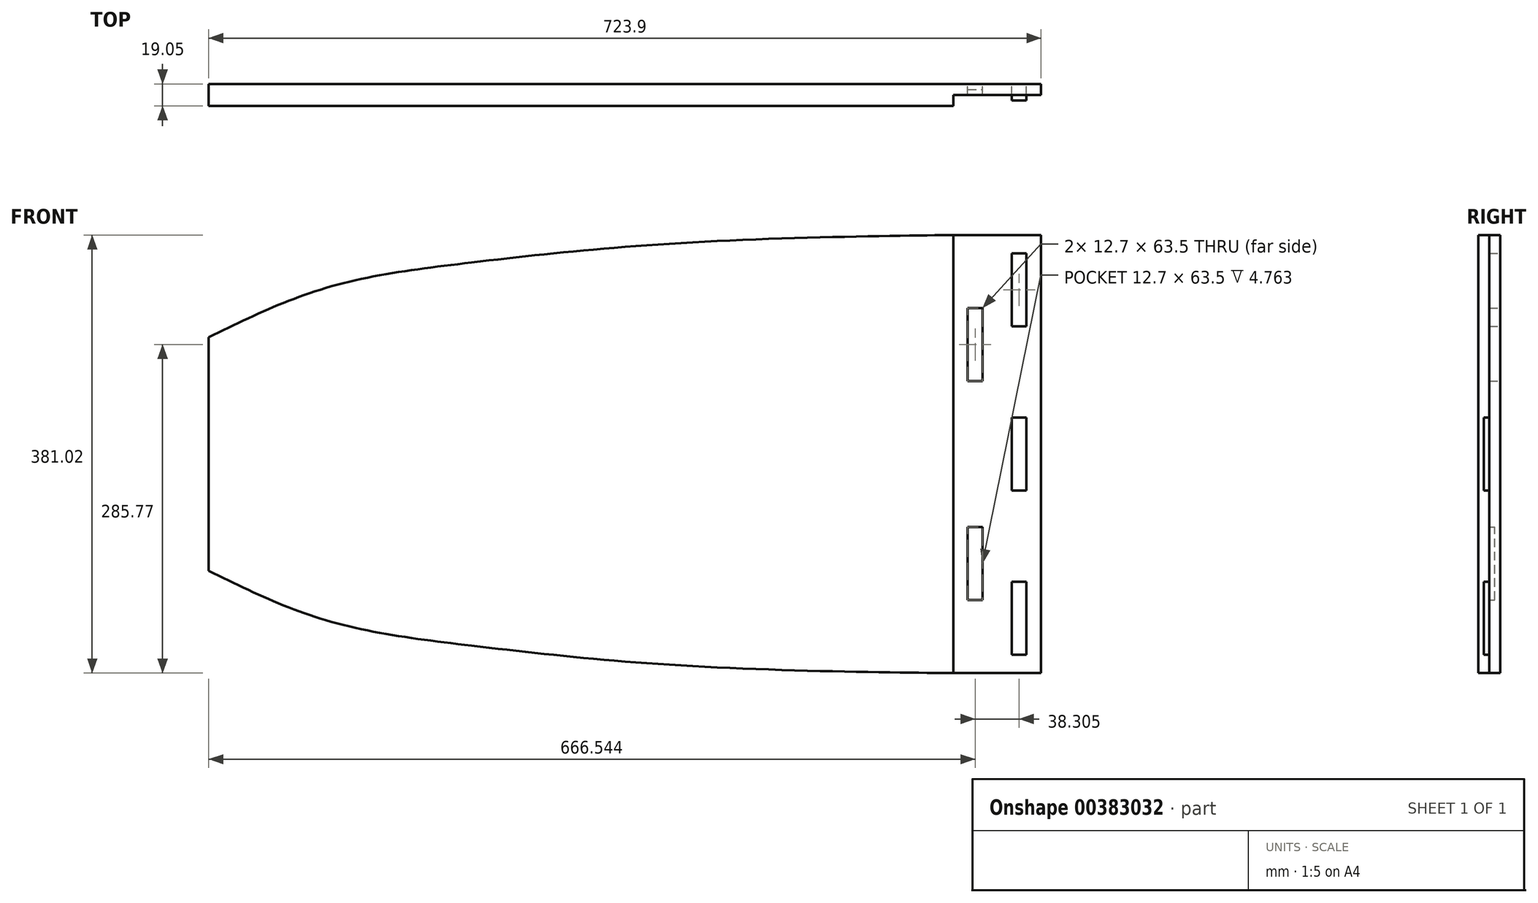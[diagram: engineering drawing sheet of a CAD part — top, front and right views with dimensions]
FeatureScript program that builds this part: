
annotation { "Feature Type Name" : "Feature", "Feature Type Description" : "" }
export const myFeature = defineFeature(function(context is Context, id is Id, definition is map)
    precondition{}
    {
        {
            var Q0;
            Q0=qCreatedBy(makeId("Front.planeOp"),FACE);
            var sketch = newSketch(context, id + "F0", { "sketchPlane" : qUnion([Q0])});
            skLineSegment(sketch, "E0", {"start": v(-290.93, -0.12) * mm, "end": v(-290.93, 184.82) * mm});
            skLineSegment(sketch, "E1", {"start": v(-290.93, -0.12) * mm, "end": v(-290.93, -185.07) * mm});
            skLineSegment(sketch, "E2", {"start": v(-493.71, 0) * mm, "end": v(-493.71, 166.69) * mm});
            skLineSegment(sketch, "E3", {"start": v(-493.71, 0) * mm, "end": v(-493.71, -166.69) * mm});
            skLineSegment(sketch, "E4", {"start": v(-620.71, 0) * mm, "end": v(-620.71, 144.46) * mm});
            skLineSegment(sketch, "E5", {"start": v(-620.71, 0) * mm, "end": v(-620.71, -144.46) * mm});
            skLineSegment(sketch, "E6", {"start": v(-722.31, 0) * mm, "end": v(-620.71, 0) * mm});
            skLineSegment(sketch, "E7", {"start": v(-722.31, 0) * mm, "end": v(-722.31, 101.6) * mm});
            skLineSegment(sketch, "E8", {"start": v(-722.31, 0) * mm, "end": v(-722.31, -101.6) * mm});
            skLineSegment(sketch, "E9", {"start": v(-36.72, 0) * mm, "end": v(-74.82, 0) * mm});
            skLineSegment(sketch, "E10", {"start": v(-36.72, 0) * mm, "end": v(-55.77, 0) * mm});
            skLineSegment(sketch, "E11", {"start": v(-36.51, 0) * mm, "end": v(1.59, 0) * mm});
            skLineSegment(sketch, "E12", {"start": v(-74.82, 0) * mm, "end": v(-74.82, 190.5) * mm});
            skLineSegment(sketch, "E13", {"start": v(-620.71, 0) * mm, "end": v(-493.71, 0) * mm});
            skLineSegment(sketch, "E14", {"start": v(-722.31, 0) * mm, "end": v(1.59, 0) * mm});
            skLineSegment(sketch, "E15", {"start": v(-36.51, 0) * mm, "end": v(-17.46, 0) * mm});
            skLineSegment(sketch, "E16", {"start": v(-36.51, 0) * mm, "end": v(-36.51, 190.5) * mm});
            skLineSegment(sketch, "E17", {"start": v(-74.82, 190.5) * mm, "end": v(1.59, 190.5) * mm});
            skLineSegment(sketch, "E18", {"start": v(-55.77, 0) * mm, "end": v(-55.77, 190.5) * mm});
            skLineSegment(sketch, "E19", {"start": v(-55.77, 0) * mm, "end": v(-55.77, 95.25) * mm});
            skLineSegment(sketch, "E20.bottom", {"start": v(-62.12, 127) * mm, "end": v(-49.42, 127) * mm});
            skLineSegment(sketch, "E20.top", {"start": v(-62.12, 63.5) * mm, "end": v(-49.42, 63.5) * mm});
            skLineSegment(sketch, "E20.left", {"start": v(-62.12, 127) * mm, "end": v(-62.12, 63.5) * mm});
            skLineSegment(sketch, "E20.right", {"start": v(-49.42, 127) * mm, "end": v(-49.42, 63.5) * mm});
            skPoint(sketch, "E20.middle", {"position": v(-55.77, 95.25) * mm});
            skLineSegment(sketch, "E21", {"start": v(-17.46, 0) * mm, "end": v(-17.46, 190.5) * mm});
            skLineSegment(sketch, "E22", {"start": v(-17.46, 0) * mm, "end": v(-17.46, 95.25) * mm});
            skLineSegment(sketch, "E23", {"start": v(-17.46, 95.25) * mm, "end": v(-17.46, 190.5) * mm});
            skLineSegment(sketch, "E24", {"start": v(-17.46, 142.88) * mm, "end": v(-17.46, 190.5) * mm});
            skLineSegment(sketch, "E25.bottom", {"start": v(-11.11, 111.13) * mm, "end": v(-23.81, 111.13) * mm});
            skLineSegment(sketch, "E25.top", {"start": v(-11.11, 174.63) * mm, "end": v(-23.81, 174.63) * mm});
            skLineSegment(sketch, "E25.left", {"start": v(-11.11, 111.13) * mm, "end": v(-11.11, 174.63) * mm});
            skLineSegment(sketch, "E25.right", {"start": v(-23.81, 111.13) * mm, "end": v(-23.81, 174.63) * mm});
            skPoint(sketch, "E25.middle", {"position": v(-17.46, 142.88) * mm});
            skLineSegment(sketch, "E26.bottom", {"start": v(-23.81, 31.75) * mm, "end": v(-11.11, 31.75) * mm});
            skLineSegment(sketch, "E26.top", {"start": v(-23.81, -31.75) * mm, "end": v(-11.11, -31.75) * mm});
            skLineSegment(sketch, "E26.left", {"start": v(-23.81, 31.75) * mm, "end": v(-23.81, -31.75) * mm});
            skLineSegment(sketch, "E26.right", {"start": v(-11.11, 31.75) * mm, "end": v(-11.11, -31.75) * mm});
            skPoint(sketch, "E26.middle", {"position": v(-17.46, 0) * mm});
            skLineSegment(sketch, "E27", {"start": v(-55.77, 0) * mm, "end": v(-55.77, 63.5) * mm});
            skLineSegment(sketch, "E28", {"start": v(-17.46, 111.13) * mm, "end": v(-17.46, 31.75) * mm});
            skLineSegment(sketch, "E29.MirrorCS", {"start": v(-55.77, 0) * mm, "end": v(-55.77, -63.5) * mm});
            skLineSegment(sketch, "E30.MirrorCS", {"start": v(-74.82, 0) * mm, "end": v(-74.82, -190.5) * mm});
            skLineSegment(sketch, "E31.MirrorCS", {"start": v(-62.12, -127) * mm, "end": v(-62.12, -63.5) * mm});
            skLineSegment(sketch, "E32.MirrorCS", {"start": v(-49.42, -127) * mm, "end": v(-49.42, -63.5) * mm});
            skLineSegment(sketch, "E33.MirrorCS", {"start": v(-62.12, -127) * mm, "end": v(-49.42, -127) * mm});
            skLineSegment(sketch, "E34.MirrorCS", {"start": v(-55.77, 0) * mm, "end": v(-55.77, -190.5) * mm});
            skLineSegment(sketch, "E35.MirrorCS", {"start": v(-62.12, -63.5) * mm, "end": v(-49.42, -63.5) * mm});
            skLineSegment(sketch, "E36.MirrorCS", {"start": v(-36.51, 0) * mm, "end": v(-36.51, -190.5) * mm});
            skLineSegment(sketch, "E37.MirrorCS", {"start": v(-11.11, -111.12) * mm, "end": v(-11.11, -174.62) * mm});
            skLineSegment(sketch, "E38.MirrorCS", {"start": v(-23.81, -111.12) * mm, "end": v(-23.81, -174.62) * mm});
            skLineSegment(sketch, "E39.MirrorCS", {"start": v(-17.46, -95.25) * mm, "end": v(-17.46, -190.5) * mm});
            skLineSegment(sketch, "E40.MirrorCS", {"start": v(-17.46, -111.12) * mm, "end": v(-17.46, -31.75) * mm});
            skLineSegment(sketch, "E41.MirrorCS", {"start": v(-17.46, 0) * mm, "end": v(-17.46, -95.25) * mm});
            skLineSegment(sketch, "E42.MirrorCS", {"start": v(-11.11, -111.12) * mm, "end": v(-23.81, -111.12) * mm});
            skFitSpline(sketch, "E43", {"points": [v(-722.31, -101.6) * mm, v(-620.71, -144.46) * mm, v(-493.71, -166.69) * mm, v(-290.93, -185.07) * mm, v(-74.82, -190.5) * mm, v(-55.77, -190.5) * mm, v(-36.51, -190.5) * mm, v(-17.46, -190.5) * mm, v(1.59, -190.5) * mm], "startDerivative": vector(641.91, -314.08) * mm, "endDerivative": vector(299.95, -0.02) * mm});
            skFitSpline(sketch, "E44", {"points": [v(-722.31, 101.6) * mm, v(-620.71, 144.46) * mm, v(-493.71, 166.69) * mm, v(-290.93, 184.82) * mm, v(-74.82, 190.5) * mm, v(-55.77, 190.5) * mm, v(-36.51, 190.5) * mm, v(-17.46, 190.5) * mm, v(1.59, 190.5) * mm], "startDerivative": vector(641.91, 313.96) * mm, "endDerivative": vector(299.95, 0.03) * mm});
            skLineSegment(sketch, "E45", {"start": v(1.59, -190.5) * mm, "end": v(1.59, 190.5) * mm});
            skLineSegment(sketch, "E46", {"start": v(-23.81, -174.62) * mm, "end": v(-11.11, -174.62) * mm});
            skSolve(sketch);
        }
        {
            var Q0;
            {var subQ0=sQuery(id+"F0.wireOp",EDGE,"E4");Q0=makeQuery(id+"F0.imprint","IMPRINT",FACE,{"disambiguationData":[TD([[makeQuery(id+"F0.imprint","IMPRINT",EDGE,{"derivedFrom":subQ0}),1.0]])]});}
            var Q1;
            {var subQ0=sQuery(id+"F0.wireOp",EDGE,"E2");Q1=makeQuery(id+"F0.imprint","IMPRINT",FACE,{"disambiguationData":[TD([[makeQuery(id+"F0.imprint","IMPRINT",EDGE,{"derivedFrom":subQ0}),1.0]])]});}
            var Q2;
            {var subQ0=sQuery(id+"F0.wireOp",EDGE,"E5");Q2=makeQuery(id+"F0.imprint","IMPRINT",FACE,{"disambiguationData":[TD([[makeQuery(id+"F0.imprint","IMPRINT",EDGE,{"derivedFrom":subQ0}),-1.0]])]});}
            var Q3;
            {var subQ0=sQuery(id+"F0.wireOp",EDGE,"E3");Q3=makeQuery(id+"F0.imprint","IMPRINT",FACE,{"disambiguationData":[TD([[makeQuery(id+"F0.imprint","IMPRINT",EDGE,{"derivedFrom":subQ0}),-1.0]])]});}
            var Q4;
            {var subQ4=sQuery(id+"F0.wireOp",EDGE,"E1");Q4=makeQuery(id+"F0.imprint","IMPRINT",FACE,{"disambiguationData":[TD([[makeQuery(id+"F0.imprint","IMPRINT",EDGE,{"derivedFrom":subQ4}),-1.0]])]});}
            var Q5;
            {var subQ5=sQuery(id+"F0.wireOp",EDGE,"E2");Q5=makeQuery(id+"F0.imprint","IMPRINT",FACE,{"disambiguationData":[TD([[makeQuery(id+"F0.imprint","IMPRINT",EDGE,{"derivedFrom":subQ5}),-1.0]])]});}
            var Q6;
            {var subQ5=sQuery(id+"F0.wireOp",EDGE,"E12");Q6=makeQuery(id+"F0.imprint","IMPRINT",FACE,{"disambiguationData":[TD([[makeQuery(id+"F0.imprint","IMPRINT",EDGE,{"derivedFrom":subQ5}),1.0]])]});}
            var Q7;
            {var subQ5=sQuery(id+"F0.wireOp",EDGE,"E1");Q7=makeQuery(id+"F0.imprint","IMPRINT",FACE,{"disambiguationData":[TD([[makeQuery(id+"F0.imprint","IMPRINT",EDGE,{"derivedFrom":subQ5}),1.0]])]});}
            extrude(context, id + "F1", {"entities" : qUnion([Q0, Q1, Q2, Q3, Q4, Q5, Q6, Q7]), "depth" : 19.05 * mm});
        }
        {
            var Q0;
            {var subQ4=sQuery(id+"F0.wireOp",EDGE,"E30.MirrorCS");Q0=makeQuery(id+"F0.imprint","IMPRINT",FACE,{"disambiguationData":[TD([[makeQuery(id+"F0.imprint","IMPRINT",EDGE,{"derivedFrom":subQ4}),1.0]])]});}
            var Q1;
            {var subQ1=sQuery(id+"F0.wireOp",EDGE,"E32.MirrorCS");Q1=makeQuery(id+"F0.imprint","IMPRINT",FACE,{"disambiguationData":[TD([[makeQuery(id+"F0.imprint","IMPRINT",EDGE,{"derivedFrom":subQ1}),-1.0]])]});}
            var Q2;
            {var subQ10=sQuery(id+"F0.wireOp",EDGE,"E36.MirrorCS");Q2=makeQuery(id+"F0.imprint","IMPRINT",FACE,{"disambiguationData":[TD([[makeQuery(id+"F0.imprint","IMPRINT",EDGE,{"derivedFrom":subQ10}),1.0]])]});}
            var Q3;
            {var subQ9=sQuery(id+"F0.wireOp",EDGE,"E37.MirrorCS");Q3=makeQuery(id+"F0.imprint","IMPRINT",FACE,{"disambiguationData":[TD([[makeQuery(id+"F0.imprint","IMPRINT",EDGE,{"derivedFrom":subQ9}),1.0]])]});}
            var Q4;
            {var subQ11=sQuery(id+"F0.wireOp",EDGE,"E25.left");Q4=makeQuery(id+"F0.imprint","IMPRINT",FACE,{"disambiguationData":[TD([[makeQuery(id+"F0.imprint","IMPRINT",EDGE,{"derivedFrom":subQ11}),-1.0]])]});}
            var Q5;
            {var subQ2=sQuery(id+"F0.wireOp",EDGE,"E16");Q5=makeQuery(id+"F0.imprint","IMPRINT",FACE,{"disambiguationData":[TD([[makeQuery(id+"F0.imprint","IMPRINT",EDGE,{"derivedFrom":subQ2}),-1.0]])]});}
            var Q6;
            {var subQ6=sQuery(id+"F0.wireOp",EDGE,"E16");Q6=makeQuery(id+"F0.imprint","IMPRINT",FACE,{"disambiguationData":[TD([[makeQuery(id+"F0.imprint","IMPRINT",EDGE,{"derivedFrom":subQ6}),1.0]])]});}
            var Q7;
            {var subQ6=sQuery(id+"F0.wireOp",EDGE,"E12");Q7=makeQuery(id+"F0.imprint","IMPRINT",FACE,{"disambiguationData":[TD([[makeQuery(id+"F0.imprint","IMPRINT",EDGE,{"derivedFrom":subQ6}),-1.0]])]});}
            extrude(context, id + "F2", {"entities" : qUnion([Q0, Q1, Q2, Q3, Q4, Q5, Q6, Q7]), "operationType" : NewBodyOperationType.ADD, "depth" : 9.52 * mm});
        }
        {
            var Q0;
            {var subQ0=sQuery(id+"F0.wireOp",EDGE,"E31.MirrorCS");Q0=makeQuery(id+"F0.imprint","IMPRINT",FACE,{"disambiguationData":[TD([[makeQuery(id+"F0.imprint","IMPRINT",EDGE,{"derivedFrom":subQ0}),-1.0]])]});}
            var Q1;
            {var subQ0=sQuery(id+"F0.wireOp",EDGE,"E32.MirrorCS");Q1=makeQuery(id+"F0.imprint","IMPRINT",FACE,{"disambiguationData":[TD([[makeQuery(id+"F0.imprint","IMPRINT",EDGE,{"derivedFrom":subQ0}),1.0]])]});}
            var Q2;
            {var subQ4=sQuery(id+"F0.wireOp",EDGE,"E19");Q2=makeQuery(id+"F0.imprint","IMPRINT",FACE,{"disambiguationData":[TD([[makeQuery(id+"F0.imprint","IMPRINT",EDGE,{"derivedFrom":subQ4}),1.0]])]});}
            var Q3;
            {var subQ1=sQuery(id+"F0.wireOp",EDGE,"E19");Q3=makeQuery(id+"F0.imprint","IMPRINT",FACE,{"disambiguationData":[TD([[makeQuery(id+"F0.imprint","IMPRINT",EDGE,{"derivedFrom":subQ1}),-1.0]])]});}
            extrude(context, id + "F3", {"entities" : qUnion([Q0, Q1, Q2, Q3]), "operationType" : NewBodyOperationType.ADD, "depth" : 4.76 * mm});
        }
        {
            var Q0;
            {var subQ1=sQuery(id+"F0.wireOp",EDGE,"E23");Q0=makeQuery(id+"F0.imprint","IMPRINT",FACE,{"disambiguationData":[TD([[makeQuery(id+"F0.imprint","IMPRINT",EDGE,{"derivedFrom":subQ1}),1.0]])]});}
            var Q1;
            {var subQ1=sQuery(id+"F0.wireOp",EDGE,"E23");Q1=makeQuery(id+"F0.imprint","IMPRINT",FACE,{"disambiguationData":[TD([[makeQuery(id+"F0.imprint","IMPRINT",EDGE,{"derivedFrom":subQ1}),-1.0]])]});}
            var Q2;
            {var subQ0=sQuery(id+"F0.wireOp",EDGE,"E22");Q2=makeQuery(id+"F0.imprint","IMPRINT",FACE,{"disambiguationData":[TD([[makeQuery(id+"F0.imprint","IMPRINT",EDGE,{"derivedFrom":subQ0}),1.0]])]});}
            var Q3;
            {var subQ0=sQuery(id+"F0.wireOp",EDGE,"E22");Q3=makeQuery(id+"F0.imprint","IMPRINT",FACE,{"disambiguationData":[TD([[makeQuery(id+"F0.imprint","IMPRINT",EDGE,{"derivedFrom":subQ0}),-1.0]])]});}
            var Q4;
            {var subQ3=sQuery(id+"F0.wireOp",EDGE,"E26.left");var subQ5=sQuery(id+"F0.wireOp",EDGE,"E26.top");var subQ6=makeQuery(id+"F0.imprint","INTERSECT",VERTEX,{"derivedFrom":[subQ3,subQ5]});Q4=makeQuery(id+"F0.imprint","IMPRINT",FACE,{"disambiguationData":[TD([[makeQuery(id+"F0.imprint","IMPRINT",EDGE,{"disambiguationData":[TD([[subQ6,1.0]])],"derivedFrom":subQ3}),1.0]])]});}
            var Q5;
            {var subQ3=sQuery(id+"F0.wireOp",EDGE,"E26.right");var subQ5=sQuery(id+"F0.wireOp",EDGE,"E26.top");var subQ7=makeQuery(id+"F0.imprint","INTERSECT",VERTEX,{"derivedFrom":[subQ3,subQ5]});Q5=makeQuery(id+"F0.imprint","IMPRINT",FACE,{"disambiguationData":[TD([[makeQuery(id+"F0.imprint","IMPRINT",EDGE,{"disambiguationData":[TD([[subQ7,1.0]])],"derivedFrom":subQ3}),-1.0]])]});}
            var Q6;
            {var subQ0=sQuery(id+"F0.wireOp",EDGE,"E38.MirrorCS");Q6=makeQuery(id+"F0.imprint","IMPRINT",FACE,{"disambiguationData":[TD([[makeQuery(id+"F0.imprint","IMPRINT",EDGE,{"derivedFrom":subQ0}),1.0]])]});}
            var Q7;
            {var subQ0=sQuery(id+"F0.wireOp",EDGE,"E37.MirrorCS");Q7=makeQuery(id+"F0.imprint","IMPRINT",FACE,{"disambiguationData":[TD([[makeQuery(id+"F0.imprint","IMPRINT",EDGE,{"derivedFrom":subQ0}),-1.0]])]});}
            extrude(context, id + "F4", {"entities" : qUnion([Q0, Q1, Q2, Q3, Q4, Q5, Q6, Q7]), "operationType" : NewBodyOperationType.ADD, "depth" : 14.29 * mm});
        }
    });
